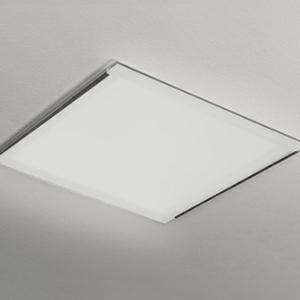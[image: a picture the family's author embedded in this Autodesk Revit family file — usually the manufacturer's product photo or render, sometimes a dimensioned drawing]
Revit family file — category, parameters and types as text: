
# Revit family: 3f_filippi_-_lucequadro_vop_3f_filippi_-_36581_-_lucequadro_led_2000_vop
name_source: partatom
category: Lighting Fixtures
units: mm (PartAtom-declared; Revit-internal decimal feet)

## family parameters
Cut with Voids When Loaded = No
Host = Face
Light Source = No
Part Type = Normal
Room Calculation Point = No
Round Connector Dimension = Use Diameter
Shared = No

## types (1)
- 3F Filippi - Lucequadro VOP (1 x LED, 1437 lm, 20 W, 4000 K)
    Apparent Load = 20 VA
    Approval mark = ENEC
    CIE Flux Codes = 47 79 96 100 100
    Color Rendering = 80
    Color Temperature = 4000 K
    Control Gear = Electronic ballast
    Default Elevation = 1800 mm
    Description = ILLUMINOTECHNICAL
Luminous efficiency 100% (DLOR 100%, ULOR 0%).
Initial luminous flux of the luminaire 1437 lm.
Direct distribution with soft, diffused and controlled light.
Installation Interdistance Transv.D = 1.25 x hu - Long.D = 1.24 x hu.
Tabular UGR (CIE 117 - 4H-8H; S=0.25H; 70/50/20): RUG 23.7 - 23.6.
Beam angle: 113° - 112°.
Luminous efficacy 72 lm/W.
Lifetime (L90/B10): 30000 h. (tq+25°C)
Lifetime (L85/B10): 50000 h. (tq+25°C)
Lifetime (L70/B10): 80000 h. (tq+25°C)
Sudden decreased luminous flux after 50000 hours: 0% (C0).
Photobiological safety in compliance with IEC/TR 62778: RG1 low risk, (IEC 62471).
In compliance with IEC/EN 62722-2-1 - IEC/EN 62717 standards.

SOURCE
Compact LED module 2000/840.
Energy efficiency class (UE 2019/2020 - UE 2019/2015): D.
CIE 13.3 Colour rendering index: CRI >80 (R9 <50%).
IES TM-30 Fidelity Index: Rf = 84 Rg = 95.
CCT nominal colour temperature 4000 K.
Colour initial tolerance (MacAdam): SDCM 3.
Zhaga Book 3 compliant.

MECHANICAL
Housing in white painted steel.
Passive heat dissipator in anodised aluminium, oversized, for optimum thermal management of the LED module.
Flow recuperator in specular aluminium with superficial titanium-magnesium treatment, non-iridescent.
Glazed opal glass, tempered, thickness 4 mm.
Lock-in mounting of the glass in the lateral seats in specular aluminium.
Fixing brackets in galvanised steel.
Slot-cover polycarbonate casings.
Dimensions: 235x235 mm, height 116 mm. Weight 2.12 kg.
IP44 protection degree for exposed part, IP20 for recessed part.
Mechanical strength to impacts IK08 (5 joule).
Glow-wire test resistance 960°C.

ELECTRICAL
Wiring on a separate unit.
Halogen Free electronic wiring 230V-50/60Hz, power factor 0.95, THD <25%, constant output current, SELV, class II, 1 driver.
Power of the luminaire 20 W.
CE - IEC 60598-1 - EN 60598-1.
SAFE FLICKER: PstLM=<1 and SVM=<0.4 (IEC TR 61547-1 and IEC TR 63158), to ensure a more comfortable and safe light.
Ambient temperature from 0°C to +25°C.
Temperature class T6 max 85°C.
Relative humidity UR: <85%.

INSTALLATION
Pull-up recessed fitting.
False ceiling carving: 210x210 mm.
All accessories dedicated to this product are available on the Catalog and on our website www.3F-Filippi.com.

ACCESSORIES
A0189 - Pair of reinforcing brackets for mineral fibre, metal and plasterboard panels, height 20 mm.

APPLICATIONS
Transit areas, corridors, commercial environments, display areas, shops and shop windows.

WARNING
Luminaire designed for disposal/recycling at end-of-life.
Replaceable (LED only) light source by a professional. Replaceable control gear by a professional.
    Height = 0 mm  [stored 0 ft]
    Lamp = 1 x LED
    Lamp Light Flux = 1437 lm
    Lamp Power = 20 W
    Lamp count = 1
    Length = 235 mm
    Lifetime = 50000 h
    Luminous efficacy = 72 lm/W
    Manufacturer = 3F Filippi
    ModVariant = No
    Model = 3F Filippi - 36581 - Lucequadro LED 2000 VOP
    Mounting Place = Ceiling
    Mounting Type = Recessed
    Number of Poles = 1
    OnlyDefault = Yes
    Power Factor = 1
    Product Name = 3F Filippi - Lucequadro VOP
    Product group = recessed luminaire
    ProductGroupID = 4
    Protection Class = Protection class II
    Protection Degree = IP 20
    RLX_Detail_Level = 1
    RLX_Emergency_Light_Flux = 0 lm
    RLX_Emergency_Type = 0
    RLX_Emergency_Type_DB = No
    RlxData = <blob elided: 54069 chars, md5=7cb92f9b>
    Socket = socket
    Standby Power = 0 W
    System Light Flux = 1437 lm
    System Power = 20 W
    Type Comments = Product without accessories
    Type Image = 3ffilippi_36581.jpg
    URL = http://relux.com
    VarID = ---
    Voltage = 0 V
    Weight = 0.00 kg
    Width = 235 mm

note: [stored X ft] marks values corroborated as IEEE doubles in the binary element streams (Revit-internal decimal feet)

## geometry (parser evidence)
native form markers: Blend x4, Sweep x12
no freeform markers — native parametric forms only
